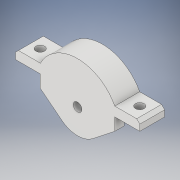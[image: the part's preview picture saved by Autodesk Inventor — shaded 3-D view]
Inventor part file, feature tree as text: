
AUTODESK INVENTOR PART (.ipt)
format: ipt  version: 2019 (Build 230136000, 136)  size: 189,952 bytes
history: native  units: mm
features: sketch x7, extrude x5, hole x2, projected_geometry x2, other x1, chamfer x1
ambient origin geometry x8: Origin, YZ Plane, XZ Plane, XY Plane, X Axis, Y Axis, Z Axis, Center Point
bodies: Body1 (feature_tree)
feature tree (18):
  other  "Твердое тело1"
  extrude  "Выдавливание1"  Depth=21.5mm
  extrude  "Выдавливание2"  Depth=0.75mm
  extrude  "Выдавливание3"  Depth=4.0mm
  hole  "Отверстие1"  [1 undecoded]
  extrude  "Выдавливание4"  Depth=3.0mm
  extrude  "Выдавливание5"  Depth=24.0mm
  hole  "Отверстие2"  [1 undecoded]
  chamfer  "Фаска1"  Distance=3.0mm
  sketch  "Эскиз1"
  sketch  "Эскиз2"
  sketch  "Эскиз3"
  projected_geometry  "Спроецированная петля1"
  projected_geometry  "Спроецированная петля2"
  sketch  "Эскиз4"
  sketch  "Эскиз5"
  sketch  "Эскиз6"
  sketch  "Эскиз7"
note: 2 required parameter values undecoded (feature->parameter linkage not recoverable at this tier; creation-order binding heuristic only, values carry confidence <= 0.55)
